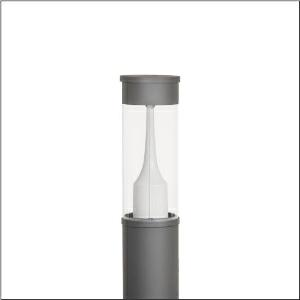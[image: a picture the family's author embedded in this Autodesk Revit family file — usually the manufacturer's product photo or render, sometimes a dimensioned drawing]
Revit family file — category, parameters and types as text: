
# Revit family: city-light_120_iq___pl1_2s_5xa5285cf14h_ce3b
name_source: partatom
category: Lighting Fixtures
units: mm (PartAtom-declared; Revit-internal decimal feet)

## family parameters
Cut with Voids When Loaded = No
Host = Face
Light Source = No
Part Type = Normal
Room Calculation Point = No
Round Connector Dimension = Use Diameter
Shared = No

## types (1)
- --- (1 x LED, 2970 lm, 23.9 W, 2200K)
    Apparent Load = 24 VA
    CIE Flux Codes = 23 62 94 96 100
    Color Rendering = 70
    Color Temperature = 2200K
    Default Elevation = 1800 mm
    Description = City-Light 120 iQ, bollard luminaire, Module 540 iQ-SR, primary light control with 3 zone facetted reflector, of plastic, silver coated, highly specular, structured, primary optical cover: cover, of PMMA, transparent, partly coated, light distribution: PL1.2s, primary light characteristic: symmetric, LED, High Power LED, rated luminous flux: 2.970lm, luminous efficacy: 124lm/W, light colour: 722, colour temperature: 2200K, control gear: ECG iQ, control: presetting dimming logarithmic, Street-Remote, Auto-Match, Temp-Guard, Lumen-Switch, Night-Set, Smart-Wire, Light-Fading, Desk-Remote (wireless, voltage-free reading and setting of iQ features in the workshop via application-optimized NFC function/RFID function), optimised constant luminous flux control (CLO 2.0), with terminal, 6-pole, max. 2.5mm², mains connection: 230..240V, AC, 50/60Hz, start of lifetime: 24W, end of service life: 26W, reduction: 12W, luminaire housing, cylindrical, of extruded aluminium section, coated, Siteco® metallic grey (DB 702S), length: 1.200mm, diameter: 200mm, Module 540 iQ-SR, traffic white (RAL 9016), equipment: standard, protection rating (complete): IP54, insulation class (complete): insulation class II (safety insulation), certification: CE, ENEC, VDE, packaging unit: 1 piece

Light Distribution: PL1.2s
    Height = 500 mm
    Lamp = 1 x LED
    Lamp Light Flux = 2970 lm
    Lamp Power = 23.9 W
    Lamp count = 1
    Length = 200 mm  [stored 0.656168 ft]
    Luminous efficacy = 124 lm/W
    Manufacturer = Siteco
    ModVariant = No
    Model = 5XA5285CF14H
    Mounting Place = Floor
    Mounting Type = Freestanding
    Number of Poles = 1
    OnlyDefault = Yes
    Power Factor = 1
    Product Name = City-Light 120 iQ | PL1.2s
    Product group = bollard luminaire
    ProductGroupID = 1304
    Protection Class = Protection class II
    Protection Degree = IP 54
    RLX_Detail_Level = 1
    RLX_Emergency_Light_Flux = 0 lm
    RLX_Emergency_Type = 0
    RLX_Emergency_Type_DB = No
    RlxData = <blob elided: 30165 chars, md5=caefdd76>
    Socket = socket
    Standby Power = 0 W
    System Light Flux = 2970 lm
    System Power = 24 W
    Type Comments = factory setting: luminous flux: 100 % | dim-lin: 254 | 499 mA
    Type Image = l_1006922.jpg
    URL = http://relux.com
    VarID = @adj_076849
    Voltage = 0 V
    Weight = 0.00 kg
    Width = 0 mm  [stored 0 ft]

note: [stored X ft] marks values corroborated as IEEE doubles in the binary element streams (Revit-internal decimal feet)

## geometry (parser evidence)
native form markers: Blend x4, Sweep x10
no freeform markers — native parametric forms only
